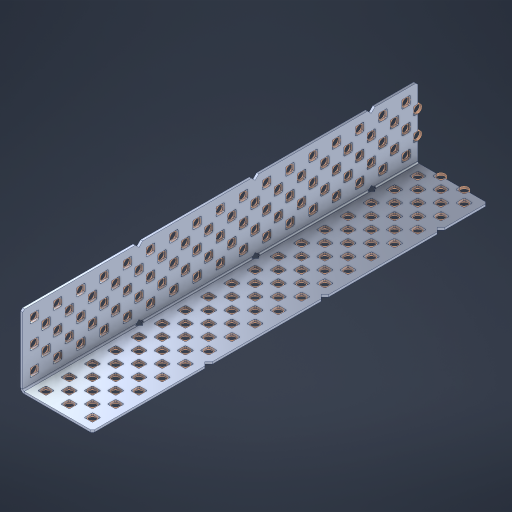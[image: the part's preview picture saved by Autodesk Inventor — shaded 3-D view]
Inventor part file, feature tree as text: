
AUTODESK INVENTOR PART (.ipt)
format: ipt  version: 2023 (Build 270158000, 158)  size: 1,935,360 bytes
history: native  units: in
note: dims shown in document units (in); Inventor stores cm internally (conversion verified against a paired STEP export)
features: other x176, extrude x168, sheet_metal_op x8, sketch x7, pattern_linear x3, mirror x1, chamfer x1
ambient origin geometry x8: Origin, YZ Plane, XZ Plane, XY Plane, X Axis, Y Axis, Z Axis, Center Point
bodies: Solid1 (feature_tree), Body (feature_tree)
feature tree (364):
  sheet_metal_op  "Flanges"
  sheet_metal_op  "Body Pattern"
  pattern_linear  "Center Double"  Spacing1=1.5in  [1 undecoded]
  pattern_linear  "Center Pattern"  Spacing1=0.1875in  [1 undecoded]
  other  "Arc Length"
  pattern_linear  "Notch Pattern"  Spacing1=0.0469in  [1 undecoded]
  other  "Diagonal Plane"
  mirror  "Everything Mirrored"
  chamfer  "End Chamfer"
  sketch  "Sketch1"  dims[d0=1.5in]
  other  "Plate1"
  sketch  "Sketch2"  dims[d1=8.5in]
  other  "Plate2"
  sheet_metal_op  "Bend1"
  sheet_metal_op  "Corner1"
  sketch  "Sketch8"  dims[d2=0.0469in]
  sketch  "Sketch9"  dims[d3=0.0469in]
  other  "Srf91"
  sheet_metal_op  "Body Pattern Sketch"
  other  "Srf92"
  sketch  "Sketch13"  dims[d4=0.0234in]
  sketch  "Sketch15"  dims[d5=0.0938in]
  sketch  "Sketch16"  dims[d6=0.0469in d7=1.5in d8=90.0deg d9=0.0312in d10=0.1875in d11=0.0469in d12=0.0469in d49=0.182in d50=0.02in d52=0.25in d53=0.0469in d54=0.0in d55=0.172in d56=1.0in d57=0.0in d85=0.1473in d86=0.1659in d89=0.0469in d90=0.0in d91=0.04in d92=0.0491in d95=2.5in d96=0.04in d97=0.25in d98=45.0deg d106=0.182in d107=0.02in d110=0.0469in d111=0.0in d112=0.172in d113=0.5in d114=0.0in d117=0.5in d126=0.0491in d127=0.1227in d128=0.08in d129=0.04in d130=2.5in d131=0.25in d132=6.6929in d134=0.5in d135=1.1811in d137=0.5in d140=0.5in d141=1.0in d142=0.3937in d144=0.5in d145=0.071in d146=0.7874in d148=0.5in]
  other  "Srf786"
  other  "Srf856"
  other  "Srf889"
  other  "Srf890"
  other  "Srf891"
  other  "Srf1275"
  other  "Srf1276"
  other  "Srf1278"
  other  "Srf1277"
  other  "Srf1285"
  other  "Srf1286"
  other  "Srf1287"
  other  "Srf1445"
  other  "Srf1446"
  other  "Srf1447"
  other  "Srf1448"
  other  "Srf1449"
  other  "Srf1537"
  other  "Srf1538"
  other  "Srf1539"
  other  "Srf1540"
  other  "Srf1541"
  other  "Srf1807"
  other  "Srf1808"
  other  "Srf1809"
  other  "Srf1810"
  other  "Srf1811"
  other  "Srf1812"
  other  "Srf1813"
  other  "Srf1814"
  other  "Srf1959"
  other  "Srf1960"
  other  "Srf1961"
  other  "Srf1962"
  other  "Srf1963"
  other  "Srf1964"
  other  "Srf1965"
  other  "Srf1966"
  other  "Srf2009"
  other  "Srf2010"
  other  "Srf2011"
  other  "Srf2012"
  other  "Srf2013"
  other  "Srf2014"
  other  "Srf2015"
  other  "Srf2016"
  other  "Srf2017"
  other  "Srf2018"
  other  "Srf2019"
  other  "Srf2020"
  other  "Srf2021"
  other  "Srf2022"
  other  "Srf2023"
  other  "Srf2024"
  other  "Srf2025"
  other  "Srf2043"
  other  "Srf2044"
  other  "Srf2045"
  other  "Srf2046"
  other  "Srf2047"
  other  "Srf2048"
  other  "Srf2049"
  other  "Srf2050"
  other  "Srf2051"
  other  "Srf2052"
  other  "Srf2053"
  other  "Srf2054"
  other  "Srf2055"
  other  "Srf2056"
  other  "Srf2057"
  other  "Srf2058"
  other  "Srf2076"
  other  "Srf2077"
  other  "Srf2078"
  other  "Srf2079"
  other  "Srf2080"
  other  "Srf2081"
  other  "Srf2082"
  other  "Srf2083"
  other  "Srf2084"
  other  "Srf2085"
  other  "Srf2086"
  other  "Srf2087"
  other  "Srf2088"
  other  "Srf2089"
  other  "Srf2090"
  other  "Srf2091"
  other  "Srf2092"
  other  "Srf2093"
  other  "Srf2094"
  other  "Srf2095"
  other  "Srf2096"
  other  "Srf2097"
  other  "Srf2098"
  other  "Srf2099"
  other  "Srf2100"
  other  "Srf2101"
  other  "Srf2102"
  other  "Srf2103"
  other  "Srf2104"
  other  "Srf2105"
  other  "Srf2106"
  other  "Srf2107"
  other  "Srf2108"
  other  "Srf2109"
  other  "Srf2110"
  other  "Srf2111"
  other  "Srf2112"
  other  "Srf2113"
  other  "Srf2114"
  other  "Srf2115"
  other  "Srf2116"
  other  "Srf2117"
  other  "Srf2118"
  other  "Srf2119"
  other  "Srf2120"
  other  "Srf2121"
  other  "Srf2122"
  other  "Srf2123"
  other  "Srf2124"
  other  "Srf2179"
  other  "Srf2180"
  other  "Srf2181"
  other  "Srf2182"
  other  "Srf2183"
  other  "Srf2184"
  other  "Srf2185"
  other  "Srf2186"
  other  "Srf2187"
  other  "Srf2188"
  other  "Srf2189"
  other  "Srf2190"
  other  "Srf2191"
  other  "Srf2192"
  other  "Srf2193"
  other  "Srf2194"
  other  "Srf2195"
  other  "Srf2196"
  other  "Srf2197"
  other  "Srf2198"
  other  "Srf2199"
  other  "Srf2200"
  other  "Srf2201"
  other  "Srf2202"
  other  "Srf2203"
  other  "Srf2204"
  other  "Srf2205"
  other  "Srf2206"
  other  "Srf2207"
  other  "Srf2208"
  other  "Srf2209"
  other  "Srf2210"
  other  "Srf2211"
  other  "Srf2212"
  other  "Srf2213"
  other  "Srf2214"
  other  "Srf2215"
  other  "Srf2216"
  other  "Srf2217"
  other  "Srf2218"
  other  "Srf2219"
  other  "Srf2220"
  other  "Srf2221"
  other  "Srf2222"
  other  "Srf2223"
  other  "Srf2224"
  other  "Srf2225"
  other  "Srf2226"
  sheet_metal_op  "Body Stamp"
  sheet_metal_op  "Body Circle"
  other  "Center Stamp"
  other  "Center Circle"
  sheet_metal_op  "Notch"
  extrude  "ExtrusionSrf92"  Depth=0.0469in
  extrude  "ExtrusionSrf856"  Depth=0.182in
  extrude  "ExtrusionSrf889"  Depth=0.02in
  extrude  "ExtrusionSrf890"  Depth=0.25in
  extrude  "ExtrusionSrf891"  Depth=0.0469in
  extrude  "ExtrusionSrf1275"  TaperAngle=0.0deg  [1 undecoded]
  extrude  "ExtrusionSrf1276"  Depth=0.5in
  extrude  "ExtrusionSrf1277"  Depth=1.0in TaperAngle=0.0deg
  extrude  "ExtrusionSrf1345"  Depth=0.5in
  extrude  "ExtrusionSrf1346"  Depth=0.5in
  extrude  "ExtrusionSrf1347"  Depth=0.0469in
  extrude  "ExtrusionSrf1348"  Depth=0.5in TaperAngle=0.0deg
  extrude  "ExtrusionSrf1445"  Depth=0.5in
  extrude  "ExtrusionSrf1446"  Depth=0.25in TaperAngle=45.0deg
  extrude  "ExtrusionSrf1447"  Depth=0.182in
  extrude  "ExtrusionSrf1448"  Depth=0.02in
  extrude  "ExtrusionSrf1449"  Depth=0.0469in
  extrude  "ExtrusionSrf1537"  TaperAngle=0.0deg  [1 undecoded]
  extrude  "ExtrusionSrf1538"  Depth=0.5in
  extrude  "ExtrusionSrf1539"  Depth=0.5in TaperAngle=0.0deg
  extrude  "ExtrusionSrf1540"  Depth=0.5in
  extrude  "ExtrusionSrf1541"  Depth=0.5in
  extrude  "ExtrusionSrf1807"  Depth=0.5in
  extrude  "ExtrusionSrf1808"  Depth=0.5in
  extrude  "ExtrusionSrf1809"  Depth=0.5in
  extrude  "ExtrusionSrf1810"  Depth=0.5in
  extrude  "ExtrusionSrf1811"  Depth=0.25in
  extrude  "ExtrusionSrf1812"  Depth=0.5in
  extrude  "ExtrusionSrf1813"  Depth=0.5in
  extrude  "ExtrusionSrf1814"  Depth=0.5in
  extrude  "ExtrusionSrf1959"  Depth=1.0in
  extrude  "ExtrusionSrf1960"  Depth=0.3937in
  extrude  "ExtrusionSrf1961"  Depth=0.5in
  extrude  "ExtrusionSrf1962"  Depth=0.5in
  extrude  "ExtrusionSrf1963"  [1 undecoded]
  extrude  "ExtrusionSrf1964"  [1 undecoded]
  extrude  "ExtrusionSrf1965"  [1 undecoded]
  extrude  "ExtrusionSrf1966"  [1 undecoded]
  extrude  "ExtrusionSrf2009"  [1 undecoded]
  extrude  "ExtrusionSrf2010"  [1 undecoded]
  extrude  "ExtrusionSrf2011"  [1 undecoded]
  extrude  "ExtrusionSrf2012"  [1 undecoded]
  extrude  "ExtrusionSrf2013"  [1 undecoded]
  extrude  "ExtrusionSrf2014"  [1 undecoded]
  extrude  "ExtrusionSrf2015"  [1 undecoded]
  extrude  "ExtrusionSrf2016"  [1 undecoded]
  extrude  "ExtrusionSrf2017"  [1 undecoded]
  extrude  "ExtrusionSrf2018"  [1 undecoded]
  extrude  "ExtrusionSrf2019"  [1 undecoded]
  extrude  "ExtrusionSrf2020"  [1 undecoded]
  extrude  "ExtrusionSrf2021"  [1 undecoded]
  extrude  "ExtrusionSrf2022"  [1 undecoded]
  extrude  "ExtrusionSrf2023"  [1 undecoded]
  extrude  "ExtrusionSrf2024"  [1 undecoded]
  extrude  "ExtrusionSrf2025"  [1 undecoded]
  extrude  "ExtrusionSrf2043"  [1 undecoded]
  extrude  "ExtrusionSrf2044"  [1 undecoded]
  extrude  "ExtrusionSrf2045"  [1 undecoded]
  extrude  "ExtrusionSrf2046"  [1 undecoded]
  extrude  "ExtrusionSrf2047"  [1 undecoded]
  extrude  "ExtrusionSrf2048"  [1 undecoded]
  extrude  "ExtrusionSrf2049"  [1 undecoded]
  extrude  "ExtrusionSrf2050"  [1 undecoded]
  extrude  "ExtrusionSrf2051"  [1 undecoded]
  extrude  "ExtrusionSrf2052"  [1 undecoded]
  extrude  "ExtrusionSrf2053"  [1 undecoded]
  extrude  "ExtrusionSrf2054"  [1 undecoded]
  extrude  "ExtrusionSrf2055"  [1 undecoded]
  extrude  "ExtrusionSrf2056"  [1 undecoded]
  extrude  "ExtrusionSrf2057"  [1 undecoded]
  extrude  "ExtrusionSrf2058"  [1 undecoded]
  extrude  "ExtrusionSrf2076"  [1 undecoded]
  extrude  "ExtrusionSrf2077"  [1 undecoded]
  extrude  "ExtrusionSrf2078"  [1 undecoded]
  extrude  "ExtrusionSrf2079"  [1 undecoded]
  extrude  "ExtrusionSrf2080"  [1 undecoded]
  extrude  "ExtrusionSrf2081"  [1 undecoded]
  extrude  "ExtrusionSrf2082"  [1 undecoded]
  extrude  "ExtrusionSrf2083"  [1 undecoded]
  extrude  "ExtrusionSrf2084"  [1 undecoded]
  extrude  "ExtrusionSrf2085"  [1 undecoded]
  extrude  "ExtrusionSrf2086"  [1 undecoded]
  extrude  "ExtrusionSrf2087"  [1 undecoded]
  extrude  "ExtrusionSrf2088"  [1 undecoded]
  extrude  "ExtrusionSrf2089"  [1 undecoded]
  extrude  "ExtrusionSrf2090"  [1 undecoded]
  extrude  "ExtrusionSrf2091"  [1 undecoded]
  extrude  "ExtrusionSrf2092"  [1 undecoded]
  extrude  "ExtrusionSrf2093"  [1 undecoded]
  extrude  "ExtrusionSrf2094"  [1 undecoded]
  extrude  "ExtrusionSrf2095"  [1 undecoded]
  extrude  "ExtrusionSrf2096"  [1 undecoded]
  extrude  "ExtrusionSrf2097"  [1 undecoded]
  extrude  "ExtrusionSrf2098"  [1 undecoded]
  extrude  "ExtrusionSrf2099"  [1 undecoded]
  extrude  "ExtrusionSrf2100"  [1 undecoded]
  extrude  "ExtrusionSrf2101"  [1 undecoded]
  extrude  "ExtrusionSrf2102"  [1 undecoded]
  extrude  "ExtrusionSrf2103"  [1 undecoded]
  extrude  "ExtrusionSrf2104"  [1 undecoded]
  extrude  "ExtrusionSrf2105"  [1 undecoded]
  extrude  "ExtrusionSrf2106"  [1 undecoded]
  extrude  "ExtrusionSrf2107"  [1 undecoded]
  extrude  "ExtrusionSrf2108"  [1 undecoded]
  extrude  "ExtrusionSrf2109"  [1 undecoded]
  extrude  "ExtrusionSrf2110"  [1 undecoded]
  extrude  "ExtrusionSrf2111"  [1 undecoded]
  extrude  "ExtrusionSrf2112"  [1 undecoded]
  extrude  "ExtrusionSrf2113"  [1 undecoded]
  extrude  "ExtrusionSrf2114"  [1 undecoded]
  extrude  "ExtrusionSrf2115"  [1 undecoded]
  extrude  "ExtrusionSrf2116"  [1 undecoded]
  extrude  "ExtrusionSrf2117"  [1 undecoded]
  extrude  "ExtrusionSrf2118"  [1 undecoded]
  extrude  "ExtrusionSrf2119"  [1 undecoded]
  extrude  "ExtrusionSrf2120"  [1 undecoded]
  extrude  "ExtrusionSrf2121"  [1 undecoded]
  extrude  "ExtrusionSrf2122"  [1 undecoded]
  extrude  "ExtrusionSrf2123"  [1 undecoded]
  extrude  "ExtrusionSrf2124"  [1 undecoded]
  extrude  "ExtrusionSrf2179"  [1 undecoded]
  extrude  "ExtrusionSrf2180"  [1 undecoded]
  extrude  "ExtrusionSrf2181"  [1 undecoded]
  extrude  "ExtrusionSrf2182"  [1 undecoded]
  extrude  "ExtrusionSrf2183"  [1 undecoded]
  extrude  "ExtrusionSrf2184"  [1 undecoded]
  extrude  "ExtrusionSrf2185"  [1 undecoded]
  extrude  "ExtrusionSrf2186"  [1 undecoded]
  extrude  "ExtrusionSrf2187"  [1 undecoded]
  extrude  "ExtrusionSrf2188"  [1 undecoded]
  extrude  "ExtrusionSrf2189"  [1 undecoded]
  extrude  "ExtrusionSrf2190"  [1 undecoded]
  extrude  "ExtrusionSrf2191"  [1 undecoded]
  extrude  "ExtrusionSrf2192"  [1 undecoded]
  extrude  "ExtrusionSrf2193"  [1 undecoded]
  extrude  "ExtrusionSrf2194"  [1 undecoded]
  extrude  "ExtrusionSrf2195"  [1 undecoded]
  extrude  "ExtrusionSrf2196"  [1 undecoded]
  extrude  "ExtrusionSrf2197"  [1 undecoded]
  extrude  "ExtrusionSrf2198"  [1 undecoded]
  extrude  "ExtrusionSrf2199"  [1 undecoded]
  extrude  "ExtrusionSrf2200"  [1 undecoded]
  extrude  "ExtrusionSrf2201"  [1 undecoded]
  extrude  "ExtrusionSrf2202"  [1 undecoded]
  extrude  "ExtrusionSrf2203"  [1 undecoded]
  extrude  "ExtrusionSrf2204"  [1 undecoded]
  extrude  "ExtrusionSrf2205"  [1 undecoded]
  extrude  "ExtrusionSrf2206"  [1 undecoded]
  extrude  "ExtrusionSrf2207"  [1 undecoded]
  extrude  "ExtrusionSrf2208"  [1 undecoded]
  extrude  "ExtrusionSrf2209"  [1 undecoded]
  extrude  "ExtrusionSrf2210"  [1 undecoded]
  extrude  "ExtrusionSrf2211"  [1 undecoded]
  extrude  "ExtrusionSrf2212"  [1 undecoded]
  extrude  "ExtrusionSrf2213"  [1 undecoded]
  extrude  "ExtrusionSrf2214"  [1 undecoded]
  extrude  "ExtrusionSrf2215"  [1 undecoded]
  extrude  "ExtrusionSrf2216"  [1 undecoded]
  extrude  "ExtrusionSrf2217"  [1 undecoded]
  extrude  "ExtrusionSrf2218"  [1 undecoded]
  extrude  "ExtrusionSrf2219"  [1 undecoded]
  extrude  "ExtrusionSrf2220"  [1 undecoded]
  extrude  "ExtrusionSrf2221"  [1 undecoded]
  extrude  "ExtrusionSrf2222"  [1 undecoded]
  extrude  "ExtrusionSrf2223"  [1 undecoded]
  extrude  "ExtrusionSrf2224"  [1 undecoded]
  extrude  "ExtrusionSrf2225"  [1 undecoded]
  extrude  "ExtrusionSrf2226"  [1 undecoded]
note: 139 required parameter values undecoded (feature->parameter linkage not recoverable at this tier; creation-order binding heuristic only, values carry confidence <= 0.55)
